# Revit family: Anschlusskombination für Hebewannen
name_source: partatom
category: Sanitärinstallationen
units: mm (PartAtom-declared; Revit-internal decimal feet)

## family parameters
Arbeitsebenenbasiert = Nein
Beim Laden mit Abzugskörper schneiden = Nein
Bemaßung runder Anschluss = Durchmesser verwenden
Gemeinsam genutzt = Nein
Immer vertikal = Ja
Raumberechnungspunkt = Nein
Teiletyp = Normal

## types (1)
- Var
    Anschlusswert DU L/s = 0
    Baugruppenkennzeichen = D2030300
    Hersteller = Resitec
    RS_AVol-H = 200 mm  [stored 0.656168 ft]
    RS_AVol-L = 129 mm  [stored 0.423228 ft]
    RS_AVol-T = 129 mm  [stored 0.423228 ft]
    RS_DN1 = 40 mm  [stored 0.131234 ft]
    RS_DN1d = 48 mm
    RS_DN2 = 70 mm  [stored 0.229659 ft]
    RS_DN2d = 78 mm  [stored 0.255906 ft]
    RS_DN50 = 50 mm  [stored 0.164042 ft]
    RS_DVol-L = 200 mm  [stored 0.656168 ft]
    RS_DVol-T = 200 mm  [stored 0.656168 ft]
    RS_Klbl = 2 mm  [stored 0.00656168 ft]
    RS_Manufacture = Resitec
    RS_RH = 297 mm  [stored 0.974409 ft]
    RS_URL = https://resitec.ch
    RS_dia001 = 113 mm  [stored 0.370735 ft]
    RS_dia002 = 130 mm  [stored 0.426509 ft]
    RS_dia19 = 19 mm  [stored 0.062336 ft]
    RS_diaDN20 = 22 mm  [stored 0.0721785 ft]
    RS_dim001 = 12 mm  [stored 0.0393701 ft]
    RS_dim002 = 22 mm  [stored 0.0721785 ft]
    RS_dim003 = 50 mm  [stored 0.164042 ft]
    RS_s = 1 mm  [stored 0.00328084 ft]
    RS_s001 = 3 mm  [stored 0.00984252 ft]
    URL = https://www.resitec.ch
    Vorgabe-Ansicht = 0 mm  [stored 0 ft]

note: [stored X ft] marks values corroborated as IEEE doubles in the binary element streams (Revit-internal decimal feet)

## geometry (parser evidence)
native form markers: Blend x8
no freeform markers — native parametric forms only
